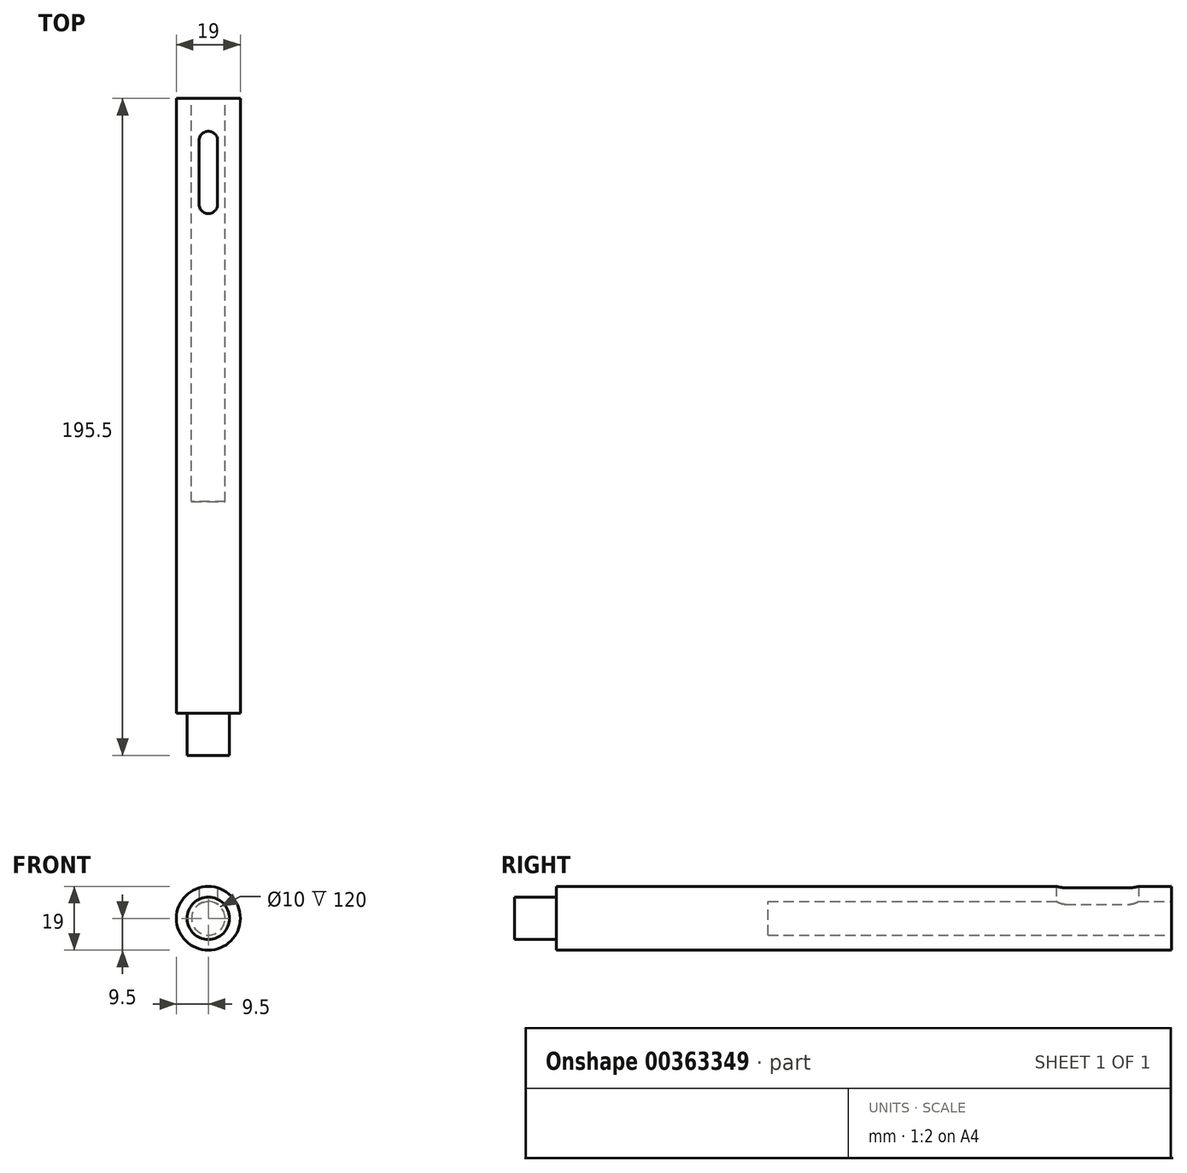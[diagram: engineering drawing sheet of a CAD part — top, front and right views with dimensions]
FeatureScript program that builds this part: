
annotation { "Feature Type Name" : "Feature", "Feature Type Description" : "" }
export const myFeature = defineFeature(function(context is Context, id is Id, definition is map)
    precondition{}
    {
        {
            var Q0;
            Q0=qCreatedBy(makeId("Front.planeOp"),FACE);
            var sketch = newSketch(context, id + "F0", { "sketchPlane" : qUnion([Q0])});
            skCircle(sketch, "E0", {"center": v(0, 0) * mm, "radius": 9.5 * mm});
            skCircle(sketch, "E1", {"center": v(0, 0) * mm, "radius": 5 * mm});
            skLineSegment(sketch, "E2", {"start": v(0, 20.65) * mm, "end": v(0, -19.38) * mm});
            skSolve(sketch);
        }
        {
            var Q0;
            {var subQ0=sQuery(id+"F0.wireOp",EDGE,"E2");var subQ1=sQuery(id+"F0.wireOp",EDGE,"E0");var subQ2=makeQuery(id+"F0.imprint","INTERSECT",VERTEX,{"disambiguationData":[OD(0.0)],"derivedFrom":[subQ1,subQ0]});Q0=makeQuery(id+"F0.imprint","IMPRINT",FACE,{"disambiguationData":[TD([[makeQuery(id+"F0.imprint","IMPRINT",EDGE,{"disambiguationData":[TD([[subQ2,-1.0]])],"derivedFrom":subQ1}),1.0]])]});}
            var Q1;
            {var subQ0=sQuery(id+"F0.wireOp",EDGE,"E2");var subQ1=sQuery(id+"F0.wireOp",EDGE,"E1");var subQ2=makeQuery(id+"F0.imprint","INTERSECT",VERTEX,{"disambiguationData":[OD(0.0)],"derivedFrom":[subQ1,subQ0]});Q1=makeQuery(id+"F0.imprint","IMPRINT",FACE,{"disambiguationData":[TD([[makeQuery(id+"F0.imprint","IMPRINT",EDGE,{"disambiguationData":[TD([[subQ2,-1.0]])],"derivedFrom":subQ1}),1.0]])]});}
            var Q2;
            {var subQ0=sQuery(id+"F0.wireOp",EDGE,"E2");var subQ1=sQuery(id+"F0.wireOp",EDGE,"E1");var subQ2=makeQuery(id+"F0.imprint","INTERSECT",VERTEX,{"disambiguationData":[OD(0.0)],"derivedFrom":[subQ1,subQ0]});Q2=makeQuery(id+"F0.imprint","IMPRINT",FACE,{"disambiguationData":[TD([[makeQuery(id+"F0.imprint","IMPRINT",EDGE,{"disambiguationData":[TD([[subQ2,1.0]])],"derivedFrom":subQ1}),1.0]])]});}
            var Q3;
            {var subQ0=sQuery(id+"F0.wireOp",EDGE,"E2");var subQ1=sQuery(id+"F0.wireOp",EDGE,"E0");var subQ2=makeQuery(id+"F0.imprint","INTERSECT",VERTEX,{"disambiguationData":[OD(0.0)],"derivedFrom":[subQ1,subQ0]});Q3=makeQuery(id+"F0.imprint","IMPRINT",FACE,{"disambiguationData":[TD([[makeQuery(id+"F0.imprint","IMPRINT",EDGE,{"disambiguationData":[TD([[subQ2,1.0]])],"derivedFrom":subQ1}),1.0]])]});}
            extrude(context, id + "F1", {"entities" : qUnion([Q0, Q1, Q2, Q3]), "depth" : 183 * mm});
        }
        {
            var Q0;
            {var subQ0=sQuery(id+"F0.wireOp",EDGE,"E2");var subQ1=sQuery(id+"F0.wireOp",EDGE,"E1");var subQ2=makeQuery(id+"F0.imprint","INTERSECT",VERTEX,{"disambiguationData":[OD(0.0)],"derivedFrom":[subQ1,subQ0]});Q0=makeQuery(id+"F0.imprint","IMPRINT",FACE,{"disambiguationData":[TD([[makeQuery(id+"F0.imprint","IMPRINT",EDGE,{"disambiguationData":[TD([[subQ2,-1.0]])],"derivedFrom":subQ1}),1.0]])]});}
            var Q1;
            {var subQ0=sQuery(id+"F0.wireOp",EDGE,"E2");var subQ1=sQuery(id+"F0.wireOp",EDGE,"E1");var subQ2=makeQuery(id+"F0.imprint","INTERSECT",VERTEX,{"disambiguationData":[OD(0.0)],"derivedFrom":[subQ1,subQ0]});Q1=makeQuery(id+"F0.imprint","IMPRINT",FACE,{"disambiguationData":[TD([[makeQuery(id+"F0.imprint","IMPRINT",EDGE,{"disambiguationData":[TD([[subQ2,1.0]])],"derivedFrom":subQ1}),1.0]])]});}
            extrude(context, id + "F2", {"entities" : qUnion([Q0, Q1]), "operationType" : NewBodyOperationType.REMOVE, "depth" : 120 * mm});
        }
        {
            var Q0;
            Q0=qCreatedBy(makeId("Top.planeOp"),FACE);
            var sketch = newSketch(context, id + "F3", { "sketchPlane" : qUnion([Q0])});
            skArc(sketch, "E3", {"start": v(2.75, -12.5) * mm, "mid": v(0, -9.75) * mm, "end": v(-2.75, -12.5) * mm});
            skArc(sketch, "E4", {"start": v(-2.75, -31.5) * mm, "mid": v(0, -34.25) * mm, "end": v(2.75, -31.5) * mm});
            skLineSegment(sketch, "E5", {"start": v(2.75, -12.5) * mm, "end": v(2.75, -31.5) * mm});
            skLineSegment(sketch, "E6", {"start": v(-2.75, -12.5) * mm, "end": v(-2.75, -31.5) * mm});
            skSolve(sketch);
        }
        {
            var Q0;
            Q0 = qSketchRegion(id + "F3", true);
            extrude(context, id + "F4", {"entities" : qUnion([Q0]), "operationType" : NewBodyOperationType.REMOVE, "depth" : 25 * mm});
        }
        {
            var Q0;
            Q0=makeQuery(id+"F1.opExtrude","CAP_FACE",FACE,{"disambiguationData":[OSD([sQuery(id+"F0.wireOp",EDGE,"E0")])],"isStart":false});
            var sketch = newSketch(context, id + "F5", { "sketchPlane" : qUnion([Q0])});
            skCircle(sketch, "E7", {"center": v(0, 0) * mm, "radius": 6.3 * mm});
            skSolve(sketch);
        }
        {
            var Q0;
            Q0=makeQuery(id+"F5.imprint","IMPRINT",FACE,{"disambiguationData":[TD([[makeQuery(id+"F5.imprint","IMPRINT",EDGE,{"derivedFrom":sQuery(id+"F5.wireOp",EDGE,"E7")}),1.0]])]});
            extrude(context, id + "F6", {"entities" : qUnion([Q0]), "operationType" : NewBodyOperationType.ADD, "depth" : 12.5 * mm});
        }
    });
